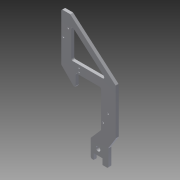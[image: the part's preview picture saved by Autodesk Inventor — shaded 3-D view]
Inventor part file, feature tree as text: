
AUTODESK INVENTOR PART (.ipt)
format: ipt  version: 2014 SP1 (Build 180222100, 222)  size: 202,752 bytes
history: native  units: in
note: dims shown in document units (in); Inventor stores cm internally (conversion verified against a paired STEP export)
features: sketch x4, extrude x4, plane x2, fillet x1
ambient origin geometry x8: Origin, YZ Plane, XZ Plane, XY Plane, X Axis, Y Axis, Z Axis, Center Point
bodies: Solid1 (feature_tree)
feature tree (11):
  sketch  "Sketch1"  dims[d0=0.25in d1=0.5in d2=0.75in d3=0.25in d5=0.3765in d6=0.5in d7=0.375in d11=1.25in d23=1.0in]
  plane  "Work Plane1"
  plane  "Work Plane2"
  extrude  "Extrusion6"  Depth=1.0in
  extrude  "Extrusion7"  Depth=1.0in
  fillet  "Fillet3"  Radius=1.5in
  extrude  "Extrusion8"  Depth=0.25in
  extrude  "Extrusion9"  Depth=1.5in
  sketch  "Sketch5"  dims[d24=1.5in d25=1.0in d26=1.5in]
  sketch  "Sketch6"  dims[d27=2.15in d32=0.25in]
  sketch  "Sketch7"  dims[d33=0.875in d34=1.5in d36=3.125in d59=4.8333in d60=4.625in d61=4.0833in d62=0.75in d64=1.25in d66=1.225in d88=0.5in d89=0.2797in d91=0.85in d92=0.75in d93=0.25in d94=0.0in d95=0.15in d96=0.15in d97=1.113in d99=0.175in d101=0.375in d102=0.0in d103=0.125in d104=0.125in d105=0.125in d106=0.1875in d107=0.25in d108=0.375in d109=0.0in d110=1.5in d111=1.5in d112=1.5in d113=0.15in d114=0.15in d115=0.906in d116=0.398in d117=0.237in d118=0.125in d119=0.375in d120=0.0in d121=10.4285in d123=0.4055in d124=0.8543in d125=0.15in d126=0.15in d127=0.4055in d128=0.8543in d129=1.625in d130=0.175in]
